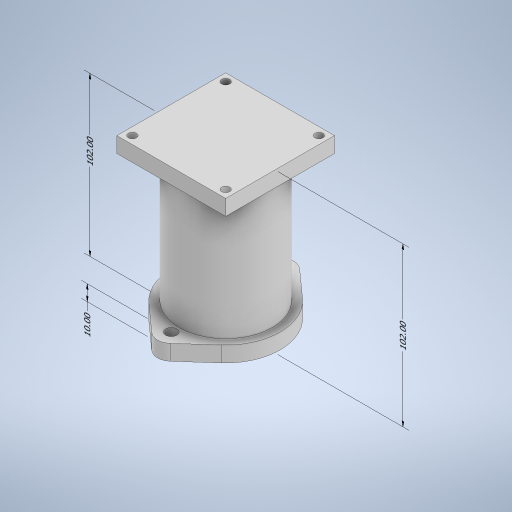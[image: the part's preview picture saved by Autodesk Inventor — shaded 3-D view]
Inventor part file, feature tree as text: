
AUTODESK INVENTOR PART (.ipt)
format: ipt  version: 2023 (Build 270158000, 158)  size: 303,104 bytes
history: native  units: mm
features: other x5, extrude x3, sketch x3
ambient origin geometry x8: Origin, YZ Plane, XZ Plane, XY Plane, X Axis, Y Axis, Z Axis, Center Point
bodies: Body1 (feature_tree)
feature tree (11):
  other  "Sólido1"
  other  "Anotaciones"
  extrude  "Extrusión1"  Depth=7.2mm
  extrude  "Extrusión2"  Depth=10.0mm TaperAngle=0.0deg
  extrude  "Extrusión3"  Depth=82.0mm TaperAngle=0.0deg
  sketch  "Boceto1"  dims[d0=65.0mm d2=7.2mm]
  sketch  "Boceto2"  dims[d3=87.0mm d5=10.0mm d6=0.0mm]
  sketch  "Boceto4"  dims[d7=60.0mm d8=82.0mm d9=0.0mm d13=70.0mm d14=70.0mm d15=60.0mm d16=5.2mm d17=5.2mm d18=5.2mm d19=5.2mm d20=10.0mm d21=0.0mm d10=8.741383mm d11=6.357805mm d12=10.0mm d22=6.285411mm d23=5.279283mm d24=102.0mm d25=5.469881mm d26=5.143145mm d27=102.0mm]
  other  "Cota lineal 1"
  other  "Cota lineal 2"
  other  "Cota lineal 3"
